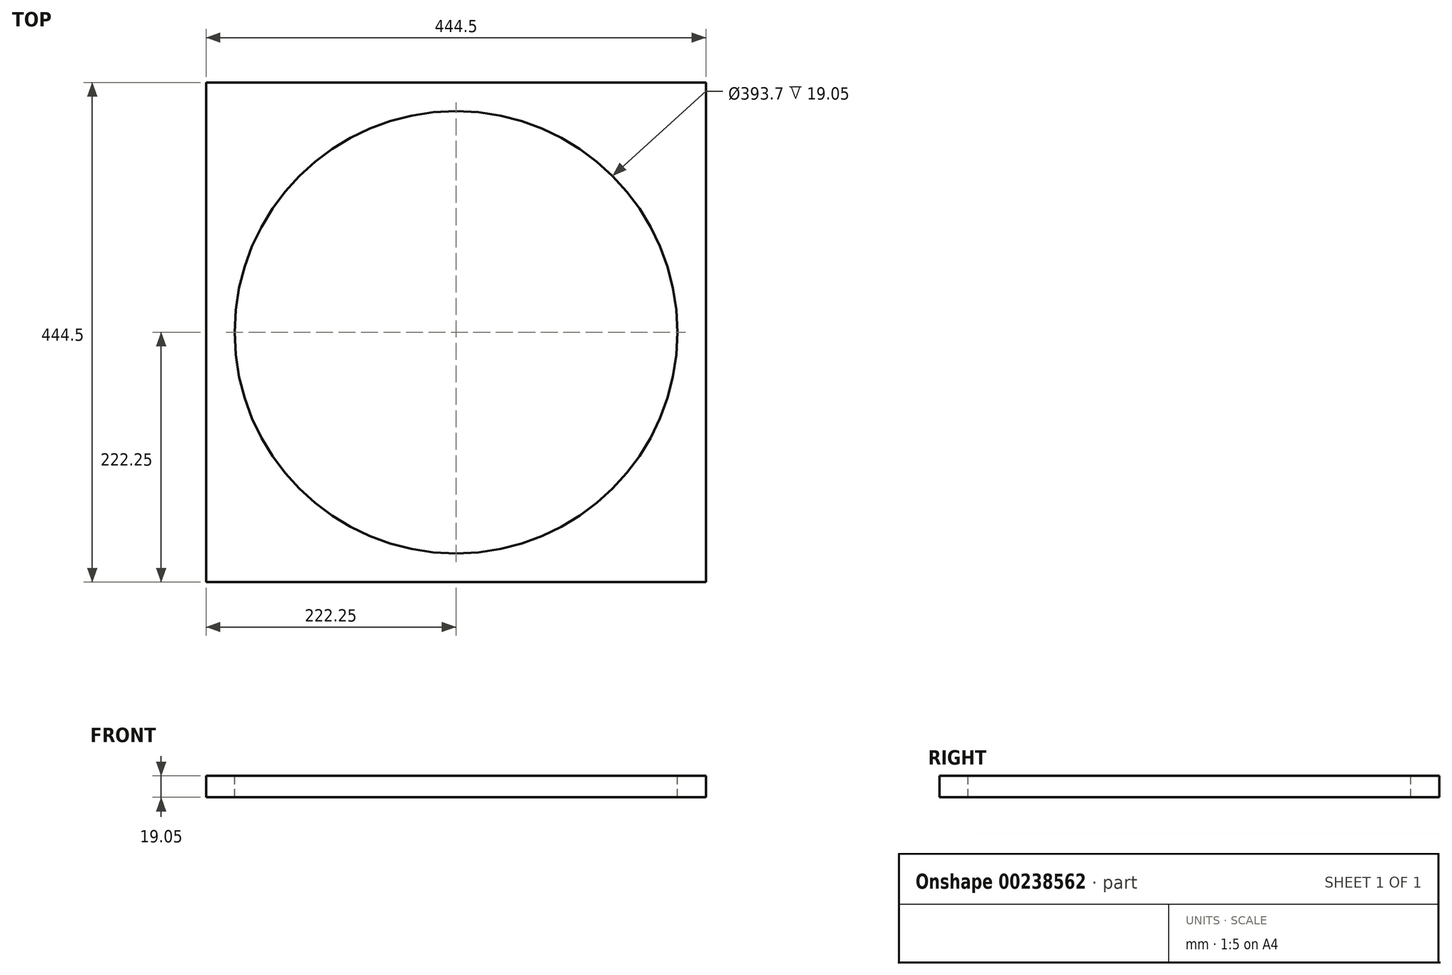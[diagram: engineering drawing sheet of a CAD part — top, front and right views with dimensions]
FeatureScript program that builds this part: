
annotation { "Feature Type Name" : "Feature", "Feature Type Description" : "" }
export const myFeature = defineFeature(function(context is Context, id is Id, definition is map)
    precondition{}
    {
        {
            var Q0;
            Q0=qCreatedBy(makeId("Top.planeOp"),FACE);
            var sketch = newSketch(context, id + "F0", { "sketchPlane" : qUnion([Q0])});
            skLineSegment(sketch, "E0.bottom", {"start": v(222.25, -222.25) * mm, "end": v(-222.25, -222.25) * mm});
            skLineSegment(sketch, "E0.top", {"start": v(222.25, 222.25) * mm, "end": v(-222.25, 222.25) * mm});
            skLineSegment(sketch, "E0.left", {"start": v(222.25, -222.25) * mm, "end": v(222.25, 222.25) * mm});
            skLineSegment(sketch, "E0.right", {"start": v(-222.25, -222.25) * mm, "end": v(-222.25, 222.25) * mm});
            skPoint(sketch, "E0.middle", {"position": v(0, 0) * mm});
            skSolve(sketch);
        }
        {
            var Q0;
            Q0=makeQuery(id+"F0.imprint","IMPRINT",FACE,{"disambiguationData":[TD([[makeQuery(id+"F0.imprint","IMPRINT",EDGE,{"derivedFrom":sQuery(id+"F0.wireOp",EDGE,"E0.bottom")}),-1.0]])]});
            extrude(context, id + "F1", {"entities" : qUnion([Q0]), "depth" : 19.05 * mm});
        }
        {
            var Q0;
            Q0=makeQuery(id+"F1.opExtrude","CAP_FACE",FACE,{"disambiguationData":[OSD([sQuery(id+"F0.wireOp",EDGE,"E0.bottom"),sQuery(id+"F0.wireOp",EDGE,"E0.top"),sQuery(id+"F0.wireOp",EDGE,"E0.left"),sQuery(id+"F0.wireOp",EDGE,"E0.right")])],"isStart":false});
            var sketch = newSketch(context, id + "F2", { "sketchPlane" : qUnion([Q0])});
            skCircle(sketch, "E1", {"center": v(0, 0) * mm, "radius": 196.85 * mm});
            skLineSegment(sketch, "E2", {"start": v(0, 222.25) * mm, "end": v(0, 0) * mm, "construction": true});
            skSolve(sketch);
        }
        {
            var Q0;
            Q0=makeQuery(id+"F2.imprint","IMPRINT",FACE,{"disambiguationData":[TD([[makeQuery(id+"F2.imprint","IMPRINT",EDGE,{"derivedFrom":sQuery(id+"F2.wireOp",EDGE,"E1")}),1.0]])]});
            extrude(context, id + "F3", {"entities" : qUnion([Q0]), "operationType" : NewBodyOperationType.REMOVE, "oppositeDirection" : true, "depth" : 25.4 * mm});
        }
    });
